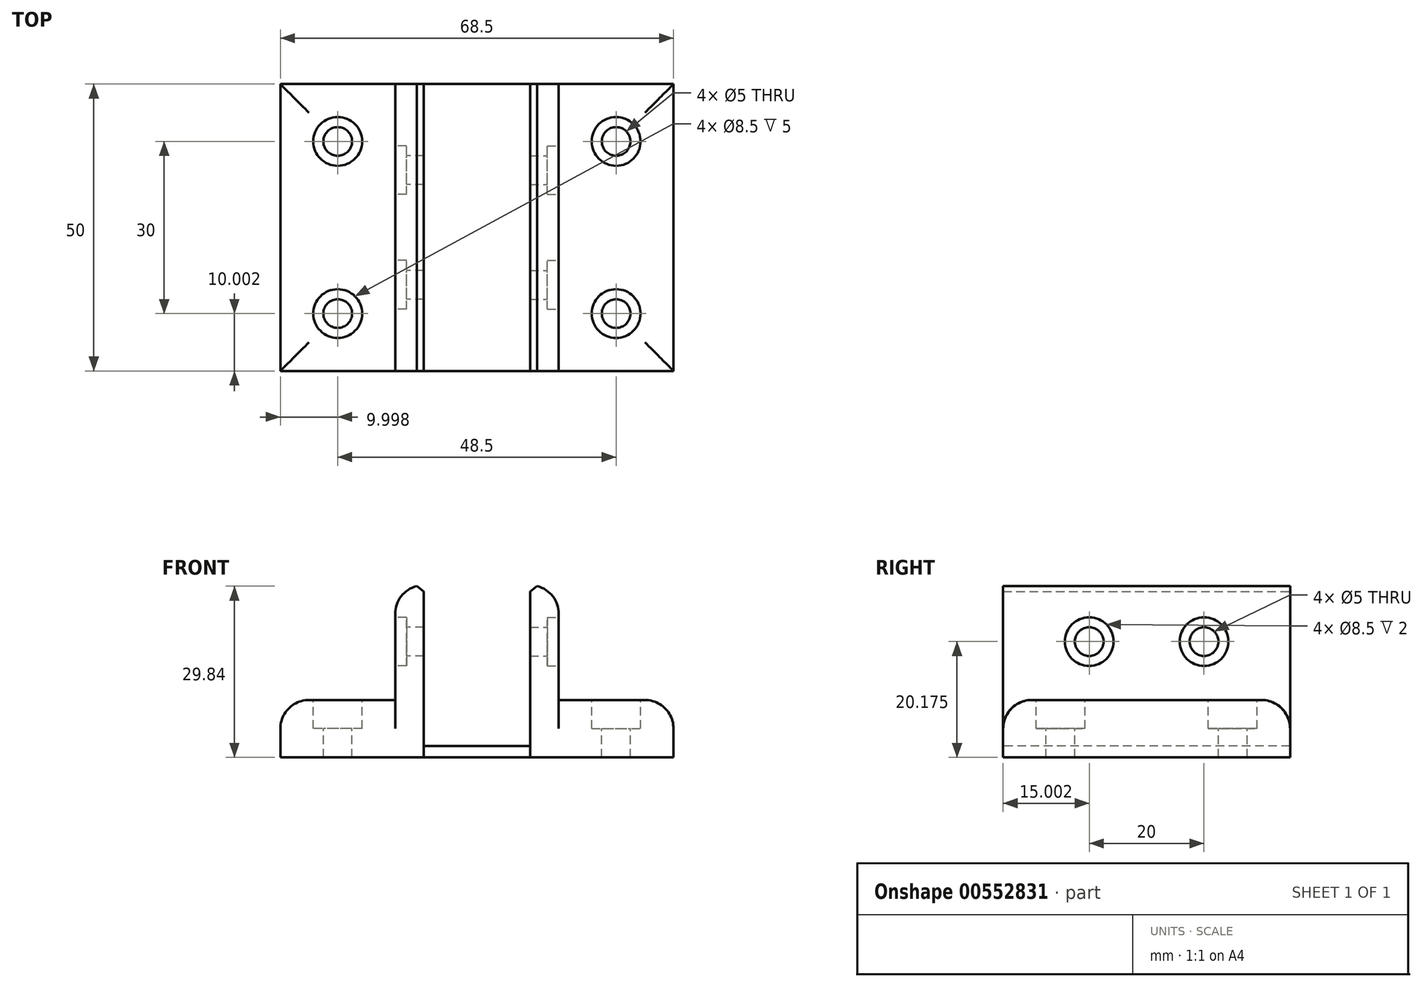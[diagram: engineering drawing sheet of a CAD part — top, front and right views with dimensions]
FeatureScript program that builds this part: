
annotation { "Feature Type Name" : "Feature", "Feature Type Description" : "" }
export const myFeature = defineFeature(function(context is Context, id is Id, definition is map)
    precondition{}
    {
        {
            var Q0;
            Q0=qCreatedBy(makeId("Top.planeOp"),FACE);
            var sketch = newSketch(context, id + "F0", { "sketchPlane" : qUnion([Q0])});
            skLineSegment(sketch, "E0.bottom", {"start": v(-22.15, 25.1) * mm, "end": v(2.85, 25.1) * mm});
            skLineSegment(sketch, "E0.top", {"start": v(-22.15, -24.9) * mm, "end": v(2.85, -24.9) * mm});
            skLineSegment(sketch, "E0.left", {"start": v(-22.15, 25.1) * mm, "end": v(-22.15, -24.9) * mm});
            skLineSegment(sketch, "E0.right", {"start": v(2.85, 25.1) * mm, "end": v(2.85, -24.9) * mm});
            skLineSegment(sketch, "E1", {"start": v(12.1, 36.03) * mm, "end": v(12.1, -31.2) * mm, "construction": true});
            skSolve(sketch);
        }
        {
            var Q0;
            Q0 = qSketchRegion(id + "F0", true);
            extrude(context, id + "F1", {"entities" : qUnion([Q0]), "depth" : 10 * mm, "offsetDistance" : 25 * mm});
        }
        {
            var Q0;
            Q0=makeQuery(id+"F1.opExtrude","CAP_FACE",FACE,{"disambiguationData":[OSD([sQuery(id+"F0.wireOp",EDGE,"E0.bottom"),sQuery(id+"F0.wireOp",EDGE,"E0.top"),sQuery(id+"F0.wireOp",EDGE,"E0.left"),sQuery(id+"F0.wireOp",EDGE,"E0.right")])],"isStart":false});
            var sketch = newSketch(context, id + "F2", { "sketchPlane" : qUnion([Q0])});
            skLineSegment(sketch, "E2.bottom", {"start": v(2.85, 25.1) * mm, "end": v(-2.15, 25.1) * mm});
            skLineSegment(sketch, "E2.top", {"start": v(2.85, -24.9) * mm, "end": v(-2.15, -24.9) * mm});
            skLineSegment(sketch, "E2.left", {"start": v(2.85, 25.1) * mm, "end": v(2.85, -24.9) * mm});
            skLineSegment(sketch, "E2.right", {"start": v(-2.15, 25.1) * mm, "end": v(-2.15, -24.9) * mm});
            skPoint(sketch, "E3", {"position": v(-12.15, 15.1) * mm});
            skPoint(sketch, "E4", {"position": v(-12.15, -14.9) * mm});
            skSolve(sketch);
        }
        {
            var Q0;
            Q0=makeQuery(id+"F2.imprint","IMPRINT",FACE,{"disambiguationData":[TD([[makeQuery(id+"F2.imprint","IMPRINT",EDGE,{"derivedFrom":sQuery(id+"F2.wireOp",EDGE,"E2.bottom")}),-1.0]])]});
            extrude(context, id + "F3", {"entities" : qUnion([Q0]), "operationType" : NewBodyOperationType.ADD, "depth" : 20 * mm, "offsetDistance" : 25 * mm});
        }
        {
            var Q0;
            Q0=sQuery(id+"F2.wireOp",VERTEX,"E3");
            var Q1;
            Q1=sQuery(id+"F2.wireOp",VERTEX,"E4");
            var Q2;
            Q2=makeQuery(id+"F1.opExtrude","SWEPT_BODY",BODY,{"disambiguationData":[OSD([sQuery(id+"F0.wireOp",EDGE,"E0.bottom"),sQuery(id+"F0.wireOp",EDGE,"E0.top"),sQuery(id+"F0.wireOp",EDGE,"E0.left"),sQuery(id+"F0.wireOp",EDGE,"E0.right")])]});
            hole(context, id + "F4", {"style" : HoleStyle.C_BORE, "endStyle" : HoleEndStyle.THROUGH, "holeDiameter" : 5 * mm, "cBoreDiameter" : 8.5 * mm, "cBoreDepth" : 5 * mm, "isTappedThrough" : true, "tappedDepth" : 12 * mm, "tapClearance" : 3, "locations" : qUnion([Q0, Q1]), "scope" : qUnion([Q2])});
        }
        {
            var Q0;
            Q0=makeQuery(id+"F1.opExtrude","CAP_EDGE",EDGE,{"disambiguationData":[OSD([sQuery(id+"F0.wireOp",EDGE,"E0.left")])],"isStart":false});
            var Q1;
            Q1=makeQuery(id+"F1.opExtrude","CAP_EDGE",EDGE,{"disambiguationData":[OSD([sQuery(id+"F0.wireOp",EDGE,"E0.top")])],"isStart":false});
            var Q2;
            Q2=makeQuery(id+"F1.opExtrude","CAP_EDGE",EDGE,{"disambiguationData":[OSD([sQuery(id+"F0.wireOp",EDGE,"E0.bottom")])],"isStart":false});
            var Q3;
            Q3=makeQuery(id+"F3.opExtrude","CAP_EDGE",EDGE,{"disambiguationData":[OSD([sQuery(id+"F2.wireOp",EDGE,"E2.right")])],"isStart":true});
            var Q4;
            Q4=makeQuery(id+"F3.opExtrude","CAP_EDGE",EDGE,{"disambiguationData":[OSD([sQuery(id+"F2.wireOp",EDGE,"E2.right")])],"isStart":false});
            fillet(context, id + "F5", {"entities" : qUnion([Q0, Q1, Q2, Q3, Q4]), "radius" : 5 * mm, "tangentPropagation" : true, "allowEdgeOverflow" : false});
        }
        {
            var Q0;
            Q0=makeQuery(id+"F3.opExtrude","SWEPT_FACE",FACE,{"disambiguationData":[OSD([sQuery(id+"F2.wireOp",EDGE,"E2.right")])]});
            var sketch = newSketch(context, id + "F6", { "sketchPlane" : qUnion([Q0])});
            skPoint(sketch, "E5", {"position": v(-10.1, 20.17) * mm});
            skPoint(sketch, "E6", {"position": v(9.9, 20.17) * mm});
            skSolve(sketch);
        }
        {
            var Q0;
            Q0=sQuery(id+"F6.wireOp",VERTEX,"E5");
            var Q1;
            Q1=sQuery(id+"F6.wireOp",VERTEX,"E6");
            var Q2;
            Q2=makeQuery(id+"F1.opExtrude","SWEPT_BODY",BODY,{"disambiguationData":[OSD([sQuery(id+"F0.wireOp",EDGE,"E0.bottom"),sQuery(id+"F0.wireOp",EDGE,"E0.top"),sQuery(id+"F0.wireOp",EDGE,"E0.left"),sQuery(id+"F0.wireOp",EDGE,"E0.right")])]});
            hole(context, id + "F7", {"style" : HoleStyle.C_BORE, "endStyle" : HoleEndStyle.THROUGH, "holeDiameter" : 5 * mm, "cBoreDiameter" : 8.5 * mm, "cBoreDepth" : 2 * mm, "isTappedThrough" : true, "tappedDepth" : 12 * mm, "tapClearance" : 3, "locations" : qUnion([Q0, Q1]), "scope" : qUnion([Q2])});
        }
        {
            var Q0;
            Q0=makeQuery(id+"F3.boolean.opBoolean","MERGE",FACE,{"derivedFrom":[makeQuery(id+"F1.opExtrude","SWEPT_FACE",FACE,{"disambiguationData":[OSD([sQuery(id+"F0.wireOp",EDGE,"E0.right")])]}),makeQuery(id+"F3.opExtrude","SWEPT_FACE",FACE,{"disambiguationData":[OSD([sQuery(id+"F2.wireOp",EDGE,"E2.left")])]})]});
            cPlane(context, id + "F8", {"entities" : qUnion([Q0]), "cplaneType" : CPlaneType.OFFSET, "offset" : 9.25 * mm, "width" : 150 * mm, "height" : 150 * mm});
        }
        {
            var Q0;
            Q0=makeQuery(id+"F1.opExtrude","SWEPT_BODY",BODY,{"disambiguationData":[OSD([sQuery(id+"F0.wireOp",EDGE,"E0.bottom"),sQuery(id+"F0.wireOp",EDGE,"E0.top"),sQuery(id+"F0.wireOp",EDGE,"E0.left"),sQuery(id+"F0.wireOp",EDGE,"E0.right")])]});
            var Q1;
            Q1=qCreatedBy(id+"F8.planeOp",FACE);
            mirror(context, id + "F9", {"operationType" : NewBodyOperationType.ADD, "entities" : qUnion([Q0]), "mirrorPlane" : qUnion([Q1])});
        }
        {
            var Q0;
            Q0=qCreatedBy(makeId("Top.planeOp"),FACE);
            var sketch = newSketch(context, id + "F10", { "sketchPlane" : qUnion([Q0])});
            skLineSegment(sketch, "E7.bottom", {"start": v(2.82, 25.1) * mm, "end": v(21.35, 25.1) * mm});
            skLineSegment(sketch, "E7.top", {"start": v(2.82, -24.9) * mm, "end": v(21.35, -24.9) * mm});
            skLineSegment(sketch, "E7.left", {"start": v(2.82, 25.1) * mm, "end": v(2.82, -24.9) * mm});
            skLineSegment(sketch, "E7.right", {"start": v(21.35, 25.1) * mm, "end": v(21.35, -24.9) * mm});
            skSolve(sketch);
        }
        {
            var Q0;
            Q0 = qSketchRegion(id + "F10", true);
            extrude(context, id + "F11", {"entities" : qUnion([Q0]), "depth" : 2 * mm, "offsetDistance" : 25 * mm});
        }
        {
            var Q0;
            Q0=makeQuery(id+"F9.opPattern","COPY",EDGE,{"derivedFrom":makeQuery(id+"F5.opFillet","BLEND_EDGE",EDGE,{"blendedFrom":[makeQuery(id+"F3.opExtrude","CAP_EDGE",EDGE,{"disambiguationData":[OSD([sQuery(id+"F2.wireOp",EDGE,"E2.right")])],"isStart":false}),makeQuery(id+"F3.boolean.opBoolean","MERGE",FACE,{"derivedFrom":[makeQuery(id+"F1.opExtrude","SWEPT_FACE",FACE,{"disambiguationData":[OSD([sQuery(id+"F0.wireOp",EDGE,"E0.right")])]}),makeQuery(id+"F3.opExtrude","SWEPT_FACE",FACE,{"disambiguationData":[OSD([sQuery(id+"F2.wireOp",EDGE,"E2.left")])]})]})],"blendedInto":[makeQuery(id+"F3.boolean.opBoolean","MERGE",FACE,{"derivedFrom":[makeQuery(id+"F1.opExtrude","SWEPT_FACE",FACE,{"disambiguationData":[OSD([sQuery(id+"F0.wireOp",EDGE,"E0.right")])]}),makeQuery(id+"F3.opExtrude","SWEPT_FACE",FACE,{"disambiguationData":[OSD([sQuery(id+"F2.wireOp",EDGE,"E2.left")])]})]})]}),"instanceName":"1"});
            var Q1;
            Q1=makeQuery(id+"F9.opPattern","COPY",EDGE,{"derivedFrom":makeQuery(id+"F5.opFillet","BLEND_EDGE",EDGE,{"blendedFrom":[makeQuery(id+"F3.opExtrude","SWEPT_EDGE",EDGE,{"disambiguationData":[OSD([sQuery(id+"F0.wireOp",EDGE,"E0.top"),sQuery(id+"F2.wireOp",EDGE,"E2.top"),sQuery(id+"F2.wireOp",EDGE,"E2.right")])]}),makeQuery(id+"F3.boolean.opBoolean","MERGE",FACE,{"derivedFrom":[makeQuery(id+"F1.opExtrude","SWEPT_FACE",FACE,{"disambiguationData":[OSD([sQuery(id+"F0.wireOp",EDGE,"E0.right")])]}),makeQuery(id+"F3.opExtrude","SWEPT_FACE",FACE,{"disambiguationData":[OSD([sQuery(id+"F2.wireOp",EDGE,"E2.left")])]})]})],"blendedInto":[makeQuery(id+"F3.boolean.opBoolean","MERGE",FACE,{"derivedFrom":[makeQuery(id+"F1.opExtrude","SWEPT_FACE",FACE,{"disambiguationData":[OSD([sQuery(id+"F0.wireOp",EDGE,"E0.right")])]}),makeQuery(id+"F3.opExtrude","SWEPT_FACE",FACE,{"disambiguationData":[OSD([sQuery(id+"F2.wireOp",EDGE,"E2.left")])]})]})]}),"instanceName":"1"});
            var Q2;
            Q2=makeQuery(id+"F9.opPattern","COPY",EDGE,{"derivedFrom":makeQuery(id+"F5.opFillet","BLEND_EDGE",EDGE,{"blendedFrom":[makeQuery(id+"F3.opExtrude","SWEPT_EDGE",EDGE,{"disambiguationData":[OSD([sQuery(id+"F0.wireOp",EDGE,"E0.bottom"),sQuery(id+"F2.wireOp",EDGE,"E2.bottom"),sQuery(id+"F2.wireOp",EDGE,"E2.right")])]}),makeQuery(id+"F3.boolean.opBoolean","MERGE",FACE,{"derivedFrom":[makeQuery(id+"F1.opExtrude","SWEPT_FACE",FACE,{"disambiguationData":[OSD([sQuery(id+"F0.wireOp",EDGE,"E0.right")])]}),makeQuery(id+"F3.opExtrude","SWEPT_FACE",FACE,{"disambiguationData":[OSD([sQuery(id+"F2.wireOp",EDGE,"E2.left")])]})]})],"blendedInto":[makeQuery(id+"F3.boolean.opBoolean","MERGE",FACE,{"derivedFrom":[makeQuery(id+"F1.opExtrude","SWEPT_FACE",FACE,{"disambiguationData":[OSD([sQuery(id+"F0.wireOp",EDGE,"E0.right")])]}),makeQuery(id+"F3.opExtrude","SWEPT_FACE",FACE,{"disambiguationData":[OSD([sQuery(id+"F2.wireOp",EDGE,"E2.left")])]})]})]}),"instanceName":"1"});
            var Q3;
            Q3=makeQuery(id+"F5.opFillet","BLEND_EDGE",EDGE,{"blendedFrom":[makeQuery(id+"F3.opExtrude","SWEPT_EDGE",EDGE,{"disambiguationData":[OSD([sQuery(id+"F0.wireOp",EDGE,"E0.bottom"),sQuery(id+"F2.wireOp",EDGE,"E2.bottom"),sQuery(id+"F2.wireOp",EDGE,"E2.right")])]}),makeQuery(id+"F3.boolean.opBoolean","MERGE",FACE,{"derivedFrom":[makeQuery(id+"F1.opExtrude","SWEPT_FACE",FACE,{"disambiguationData":[OSD([sQuery(id+"F0.wireOp",EDGE,"E0.right")])]}),makeQuery(id+"F3.opExtrude","SWEPT_FACE",FACE,{"disambiguationData":[OSD([sQuery(id+"F2.wireOp",EDGE,"E2.left")])]})]})],"blendedInto":[makeQuery(id+"F3.boolean.opBoolean","MERGE",FACE,{"derivedFrom":[makeQuery(id+"F1.opExtrude","SWEPT_FACE",FACE,{"disambiguationData":[OSD([sQuery(id+"F0.wireOp",EDGE,"E0.right")])]}),makeQuery(id+"F3.opExtrude","SWEPT_FACE",FACE,{"disambiguationData":[OSD([sQuery(id+"F2.wireOp",EDGE,"E2.left")])]})]})]});
            var Q4;
            Q4=makeQuery(id+"F5.opFillet","BLEND_EDGE",EDGE,{"blendedFrom":[makeQuery(id+"F3.opExtrude","CAP_EDGE",EDGE,{"disambiguationData":[OSD([sQuery(id+"F2.wireOp",EDGE,"E2.right")])],"isStart":false}),makeQuery(id+"F3.boolean.opBoolean","MERGE",FACE,{"derivedFrom":[makeQuery(id+"F1.opExtrude","SWEPT_FACE",FACE,{"disambiguationData":[OSD([sQuery(id+"F0.wireOp",EDGE,"E0.right")])]}),makeQuery(id+"F3.opExtrude","SWEPT_FACE",FACE,{"disambiguationData":[OSD([sQuery(id+"F2.wireOp",EDGE,"E2.left")])]})]})],"blendedInto":[makeQuery(id+"F3.boolean.opBoolean","MERGE",FACE,{"derivedFrom":[makeQuery(id+"F1.opExtrude","SWEPT_FACE",FACE,{"disambiguationData":[OSD([sQuery(id+"F0.wireOp",EDGE,"E0.right")])]}),makeQuery(id+"F3.opExtrude","SWEPT_FACE",FACE,{"disambiguationData":[OSD([sQuery(id+"F2.wireOp",EDGE,"E2.left")])]})]})]});
            var Q5;
            Q5=makeQuery(id+"F5.opFillet","BLEND_EDGE",EDGE,{"blendedFrom":[makeQuery(id+"F3.opExtrude","SWEPT_EDGE",EDGE,{"disambiguationData":[OSD([sQuery(id+"F0.wireOp",EDGE,"E0.top"),sQuery(id+"F2.wireOp",EDGE,"E2.top"),sQuery(id+"F2.wireOp",EDGE,"E2.right")])]}),makeQuery(id+"F3.boolean.opBoolean","MERGE",FACE,{"derivedFrom":[makeQuery(id+"F1.opExtrude","SWEPT_FACE",FACE,{"disambiguationData":[OSD([sQuery(id+"F0.wireOp",EDGE,"E0.right")])]}),makeQuery(id+"F3.opExtrude","SWEPT_FACE",FACE,{"disambiguationData":[OSD([sQuery(id+"F2.wireOp",EDGE,"E2.left")])]})]})],"blendedInto":[makeQuery(id+"F3.boolean.opBoolean","MERGE",FACE,{"derivedFrom":[makeQuery(id+"F1.opExtrude","SWEPT_FACE",FACE,{"disambiguationData":[OSD([sQuery(id+"F0.wireOp",EDGE,"E0.right")])]}),makeQuery(id+"F3.opExtrude","SWEPT_FACE",FACE,{"disambiguationData":[OSD([sQuery(id+"F2.wireOp",EDGE,"E2.left")])]})]})]});
            chamfer(context, id + "F12", {"entities" : qUnion([Q0, Q1, Q2, Q3, Q4, Q5]), "width" : 1 * mm, "tangentPropagation" : true});
        }
    });
